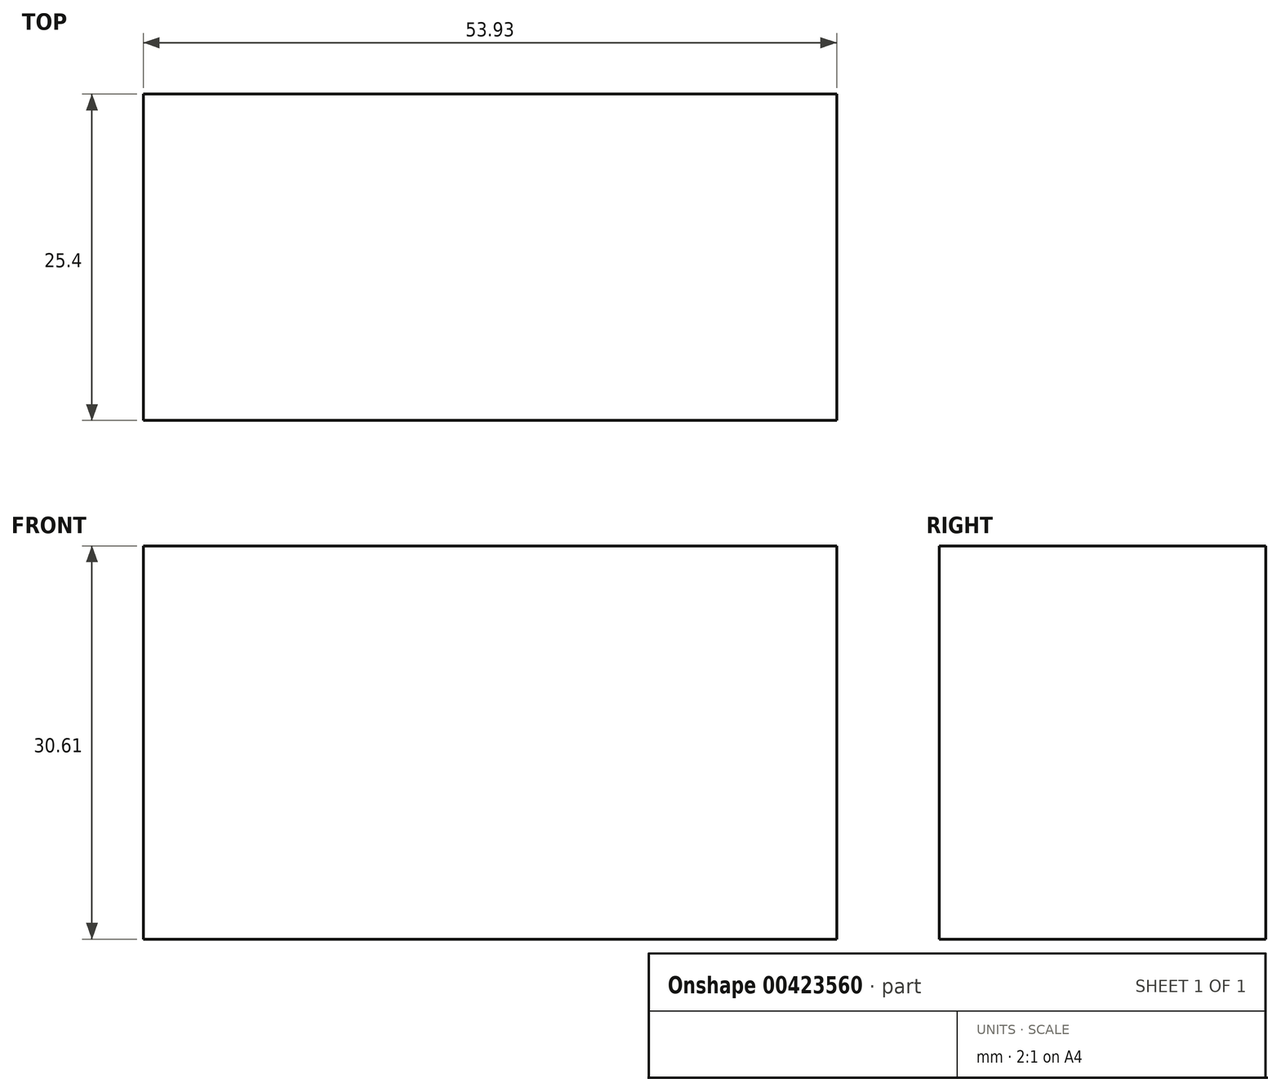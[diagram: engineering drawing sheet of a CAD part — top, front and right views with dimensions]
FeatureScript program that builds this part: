
annotation { "Feature Type Name" : "Feature", "Feature Type Description" : "" }
export const myFeature = defineFeature(function(context is Context, id is Id, definition is map)
    precondition{}
    {
        {
            var Q0;
            Q0=qCreatedBy(makeId("Front.planeOp"),FACE);
            var sketch = newSketch(context, id + "F0", { "sketchPlane" : qUnion([Q0])});
            skLineSegment(sketch, "E0.bottom", {"start": v(-19.74, 13.34) * mm, "end": v(34.2, 13.34) * mm});
            skLineSegment(sketch, "E0.top", {"start": v(-19.74, -17.27) * mm, "end": v(34.2, -17.27) * mm});
            skLineSegment(sketch, "E0.left", {"start": v(-19.74, 13.34) * mm, "end": v(-19.74, -17.27) * mm});
            skLineSegment(sketch, "E0.right", {"start": v(34.2, 13.34) * mm, "end": v(34.2, -17.27) * mm});
            skSolve(sketch);
        }
        {
            var Q0;
            Q0 = qSketchRegion(id + "F0", true);
            extrude(context, id + "F1", {"entities" : qUnion([Q0]), "depth" : 25.4 * mm});
        }
    });
